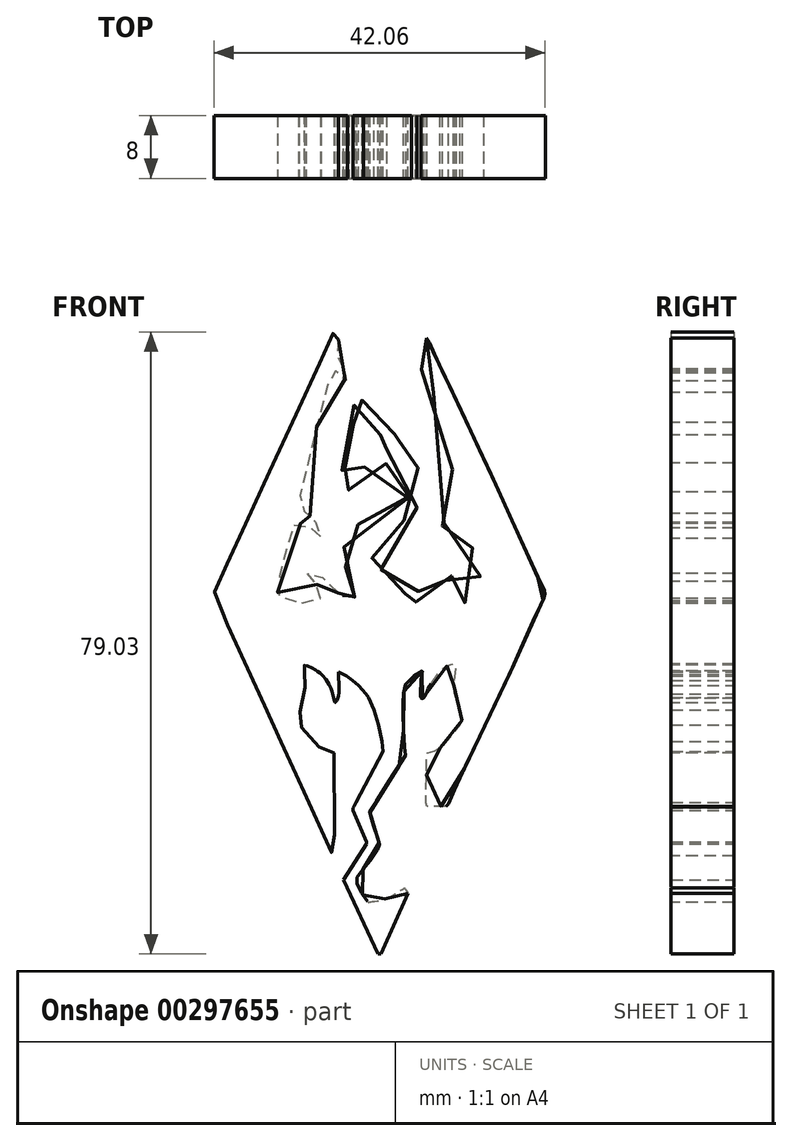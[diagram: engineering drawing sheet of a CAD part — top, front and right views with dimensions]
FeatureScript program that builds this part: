
annotation { "Feature Type Name" : "Feature", "Feature Type Description" : "" }
export const myFeature = defineFeature(function(context is Context, id is Id, definition is map)
    precondition{}
    {
        {
            var Q0;
            Q0=qCreatedBy(makeId("Front.planeOp"),FACE);
            var sketch = newSketch(context, id + "F0", { "sketchPlane" : qUnion([Q0])});
            skLineSegment(sketch, "E0", {"start": v(-80, 80.48) * mm, "end": v(-80, 0) * mm});
            skLineSegment(sketch, "E1", {"start": v(-80, 0) * mm, "end": v(0, 0) * mm});
            skLineSegment(sketch, "E2", {"start": v(0, 0) * mm, "end": v(0, 82.9) * mm});
            skLineSegment(sketch, "E3", {"start": v(0, 82.9) * mm, "end": v(-80, 80.48) * mm});
            skLineSegment(sketch, "E4", {"start": v(-24.18, 7.7) * mm, "end": v(-27.61, 0) * mm});
            skLineSegment(sketch, "E5", {"start": v(-27.61, 0) * mm, "end": v(-27.98, 0) * mm});
            skLineSegment(sketch, "E6", {"start": v(-27.98, 0) * mm, "end": v(-32.38, 9.42) * mm});
            skLineSegment(sketch, "E7", {"start": v(-32.38, 9.42) * mm, "end": v(-31.33, 11.07) * mm});
            skLineSegment(sketch, "E8", {"start": v(-31.33, 11.07) * mm, "end": v(-29.48, 13.96) * mm});
            skLineSegment(sketch, "E9", {"start": v(-29.48, 14.25) * mm, "end": v(-29.48, 13.96) * mm});
            skLineSegment(sketch, "E10", {"start": v(-29.48, 14.25) * mm, "end": v(-31.07, 18.02) * mm});
            skLineSegment(sketch, "E11", {"start": v(-31.07, 18.02) * mm, "end": v(-31.16, 18.24) * mm});
            skLineSegment(sketch, "E12", {"start": v(-31.16, 18.24) * mm, "end": v(-31.16, 18.45) * mm});
            skLineSegment(sketch, "E13", {"start": v(-31.16, 18.45) * mm, "end": v(-31.16, 18.6) * mm});
            skLineSegment(sketch, "E14", {"start": v(-31.16, 18.6) * mm, "end": v(-31.07, 18.79) * mm});
            skLineSegment(sketch, "E15", {"start": v(-31.07, 18.79) * mm, "end": v(-30.8, 19.3) * mm});
            skLineSegment(sketch, "E16", {"start": v(-30.8, 19.3) * mm, "end": v(-28.86, 22.93) * mm});
            skLineSegment(sketch, "E17", {"start": v(-28.86, 22.93) * mm, "end": v(-27.47, 25.54) * mm});
            skLineSegment(sketch, "E18", {"start": v(-27.47, 25.54) * mm, "end": v(-27.38, 25.7) * mm});
            skLineSegment(sketch, "E19", {"start": v(-27.38, 25.7) * mm, "end": v(-27.52, 27) * mm});
            skLineSegment(sketch, "E20", {"start": v(-27.52, 27) * mm, "end": v(-27.94, 29.12) * mm});
            skLineSegment(sketch, "E21", {"start": v(-27.94, 29.12) * mm, "end": v(-28.54, 31.02) * mm});
            skLineSegment(sketch, "E22", {"start": v(-28.54, 31.02) * mm, "end": v(-29.21, 32.62) * mm});
            skLineSegment(sketch, "E23", {"start": v(-29.21, 32.62) * mm, "end": v(-29.54, 33.06) * mm});
            skLineSegment(sketch, "E24", {"start": v(-29.54, 33.06) * mm, "end": v(-30.51, 34.14) * mm});
            skLineSegment(sketch, "E25", {"start": v(-30.51, 34.14) * mm, "end": v(-31.27, 34.78) * mm});
            skLineSegment(sketch, "E26", {"start": v(-31.27, 34.78) * mm, "end": v(-32.03, 35.3) * mm});
            skLineSegment(sketch, "E27", {"start": v(-32.03, 35.3) * mm, "end": v(-32.37, 35.52) * mm});
            skLineSegment(sketch, "E28", {"start": v(-32.37, 35.52) * mm, "end": v(-33.04, 35.8) * mm});
            skLineSegment(sketch, "E29", {"start": v(-33.04, 35.8) * mm, "end": v(-33.04, 35.52) * mm});
            skFitSpline(sketch, "E30", {"points": [v(-33.04, 35.52) * mm, v(-32.98, 34.7) * mm, v(-32.96, 34.28) * mm, v(-32.95, 33.57) * mm, v(-32.99, 33.2) * mm, v(-33.1, 32.52) * mm, v(-33.44, 31.92) * mm, v(-33.55, 32.17) * mm, v(-33.77, 33.03) * mm, v(-33.95, 33.58) * mm, v(-34.23, 34.24) * mm, v(-35.06, 35.42) * mm, v(-35.42, 35.72) * mm, v(-35.72, 35.94) * mm, v(-36.01, 36.14) * mm, v(-36.88, 36.6) * mm, v(-37.35, 36.68) * mm, v(-37.34, 36.34) * mm, v(-37.33, 35.98) * mm], "startDerivative": vector(1.1, -13.67) * mm, "endDerivative": vector(-0.4, -7.76) * mm});
            skFitSpline(sketch, "E31", {"points": [v(-37.33, 35.98) * mm, v(-37.29, 35.2) * mm, v(-37.3, 34.9) * mm, v(-37.3, 33.86) * mm, v(-37.55, 32.48) * mm, v(-37.95, 30.55) * mm, v(-38.08, 30.04) * mm, v(-38.02, 29.4) * mm, v(-37.45, 28.4) * mm, v(-35.92, 26.66) * mm, v(-35, 26.05) * mm, v(-33.88, 25.65) * mm, v(-33.68, 25.62) * mm, v(-33.6, 25.5) * mm, v(-33.56, 24.38) * mm, v(-33.57, 22.1) * mm, v(-33.56, 19.26) * mm, v(-33.56, 16.86) * mm, v(-33.57, 15.3) * mm, v(-33.59, 12.55) * mm, v(-33.7, 12.5) * mm, v(-34.23, 13.62) * mm, v(-34.61, 14.45) * mm, v(-36.12, 17.77) * mm, v(-37.28, 20.27) * mm, v(-37.7, 21.24) * mm, v(-39.07, 24.23) * mm, v(-40.42, 27.19) * mm, v(-41.69, 30) * mm, v(-48.6, 45) * mm, v(-48.82, 45.7) * mm, v(-48.48, 46.87) * mm, v(-47.1, 49.7) * mm, v(-44.84, 54.6) * mm, v(-40.78, 63.44) * mm, v(-36.52, 72.67) * mm, v(-34.17, 77.84) * mm, v(-33.71, 78.9) * mm, v(-33.66, 78.99) * mm, v(-33.6, 79.03) * mm, v(-33.46, 78.93) * mm, v(-33.04, 78.2) * mm, v(-33.03, 78.07) * mm, v(-33.19, 77.47) * mm, v(-33.22, 77.05) * mm, v(-33.2, 76.03) * mm, v(-32.87, 75.2) * mm, v(-32.62, 74.78) * mm, v(-32.14, 74) * mm, v(-31.95, 73.61) * mm, v(-31.9, 73.24) * mm, v(-32, 72.82) * mm, v(-32.05, 72.81) * mm, v(-32.36, 73.33) * mm, v(-32.86, 73.85) * mm, v(-33.24, 74.06) * mm, v(-34.01, 73.82) * mm, v(-34.36, 72.94) * mm, v(-34.5, 71.9) * mm, v(-35.29, 68.9) * mm, v(-36.16, 65.5) * mm, v(-37.52, 59.86) * mm, v(-38, 57.65) * mm, v(-37.95, 57.04) * mm, v(-37.54, 56.43) * mm, v(-36.92, 55.87) * mm, v(-36.46, 55.5) * mm, v(-36.02, 55) * mm, v(-35.6, 54.43) * mm, v(-35.32, 53.67) * mm, v(-35.29, 53.11) * mm, v(-35.36, 52.79) * mm, v(-36.14, 53.74) * mm, v(-36.55, 54.12) * mm, v(-37.4, 54.59) * mm, v(-38.14, 54.7) * mm, v(-38.8, 54.36) * mm, v(-39.09, 53.57) * mm, v(-39.5, 51.83) * mm, v(-40.14, 49.41) * mm, v(-40.77, 46.9) * mm, v(-40.76, 45.95) * mm, v(-40.58, 45.52) * mm, v(-39.53, 44.85) * mm, v(-37.8, 44.57) * mm, v(-36.5, 44.7) * mm, v(-35.43, 45.14) * mm, v(-35.23, 45.3) * mm, v(-35.34, 46.05) * mm, v(-35.8, 47) * mm, v(-36.94, 48.09) * mm, v(-37.15, 48.2) * mm, v(-37.17, 48.26) * mm, v(-37.11, 48.3) * mm, v(-36.92, 48.32) * mm, v(-36.63, 48.3) * mm, v(-36.24, 48.24) * mm, v(-35.15, 47.85) * mm, v(-34.71, 47.6) * mm, v(-33.55, 46.55) * mm, v(-32.76, 45.3) * mm, v(-32.52, 44.85) * mm, v(-32.5, 45.08) * mm, v(-32.6, 45.86) * mm, v(-33.03, 47.07) * mm, v(-33.18, 47.3) * mm, v(-33.14, 47.33) * mm, v(-32.96, 47.32) * mm, v(-31.78, 46.5) * mm, v(-31.39, 46.03) * mm, v(-30.87, 45.18) * mm, v(-30.84, 45.16) * mm, v(-30.8, 45.2) * mm, v(-30.85, 45.47) * mm, v(-30.94, 45.92) * mm, v(-31.37, 47.14) * mm, v(-31.6, 47.7) * mm, v(-32.1, 49.03) * mm, v(-32.27, 49.77) * mm, v(-32.4, 50.67) * mm, v(-32.14, 52.44) * mm, v(-31.11, 54.04) * mm, v(-30.16, 54.76) * mm, v(-27.34, 55.99) * mm, v(-27.32, 55.97) * mm, v(-25.95, 56.54) * mm, v(-24.17, 57.9) * mm, v(-23.9, 58.63) * mm, v(-23.8, 59.6) * mm, v(-24.2, 60.66) * mm, v(-25.45, 61.8) * mm, v(-27.07, 62.3) * mm, v(-28.93, 62.28) * mm, v(-30.29, 61.35) * mm, v(-31.73, 59.56) * mm, v(-31.71, 59.16) * mm, v(-31.82, 58.83) * mm, v(-32.07, 58.72) * mm, v(-32.42, 58.98) * mm, v(-32.82, 59.56) * mm, v(-32.94, 60.42) * mm, v(-32.93, 61.08) * mm, v(-32.43, 61.6) * mm, v(-32.07, 62.1) * mm, v(-32.2, 63.44) * mm, v(-32.06, 63.88) * mm, v(-30.81, 66.02) * mm, v(-30.83, 66.11) * mm, v(-31.14, 67.52) * mm, v(-31.08, 69.33) * mm, v(-30.77, 70.55) * mm, v(-30.18, 71.15) * mm, v(-29.87, 71.31) * mm, v(-29.96, 70.95) * mm, v(-30, 68.91) * mm, v(-29.33, 67.01) * mm, v(-28.97, 66.13) * mm, v(-26.27, 66.02) * mm, v(-24.74, 66.37) * mm, v(-24.14, 67) * mm, v(-23.89, 67.52) * mm, v(-23.84, 66.58) * mm, v(-25.13, 65.44) * mm, v(-26.81, 64.31) * mm, v(-26.93, 63.97) * mm, v(-26.38, 63.74) * mm, v(-24.05, 62.75) * mm, v(-22.63, 61.29) * mm, v(-22.24, 59.6) * mm, v(-22.4, 58.14) * mm, v(-23.9, 55.67) * mm, v(-26.38, 54.44) * mm, v(-28.06, 53.6) * mm, v(-29.13, 52.16) * mm, v(-28.84, 50.4) * mm, v(-26.98, 48.2) * mm, v(-25.69, 46.75) * mm, v(-24.9, 45.15) * mm, v(-24.49, 45.8) * mm, v(-23.23, 47.06) * mm, v(-22.49, 47.3) * mm, v(-22.56, 46.86) * mm, v(-23.27, 44.97) * mm, v(-23.29, 44.63) * mm, v(-22.9, 45.27) * mm, v(-21.8, 46.93) * mm, v(-19.72, 48.18) * mm, v(-18.48, 48.26) * mm, v(-18.7, 48.03) * mm, v(-20.08, 46.63) * mm, v(-20.22, 45.45) * mm, v(-20.19, 45.32) * mm, v(-18.46, 44.66) * mm, v(-16.2, 44.83) * mm, v(-14.7, 46) * mm, v(-15.32, 48.8) * mm, v(-16.09, 51.97) * mm, v(-16.73, 54.24) * mm, v(-17.16, 54.64) * mm, v(-18.1, 54.77) * mm, v(-19.81, 54.13) * mm, v(-19.31, 55.22) * mm, v(-17.91, 56.7) * mm, v(-17.77, 58.71) * mm, v(-18.74, 62.38) * mm, v(-21.58, 73.61) * mm, v(-22.03, 74.25) * mm, v(-22.62, 74.18) * mm, v(-22.98, 73.8) * mm, v(-23, 74.42) * mm, v(-22.45, 75.67) * mm, v(-22.56, 77.26) * mm, v(-21.88, 78.27) * mm, v(-21.35, 77.4) * mm, v(-15.69, 65.35) * mm, v(-6.79, 45.97) * mm, v(-6.77, 45.93) * mm, v(-6.85, 45.4) * mm, v(-6.97, 45.17) * mm, v(-11.44, 35.34) * mm, v(-19.12, 18.83) * mm, v(-19.15, 18.76) * mm, v(-21.8, 18.74) * mm, v(-21.88, 18.74) * mm, v(-21.84, 25.54) * mm, v(-21.84, 25.56) * mm, v(-20.46, 25.94) * mm, v(-17.97, 28.65) * mm, v(-17.37, 29.66) * mm, v(-18.16, 32.55) * mm, v(-18.31, 34.82) * mm, v(-18.24, 36.8) * mm, v(-20.56, 35.45) * mm, v(-22.31, 32.47) * mm, v(-22.52, 32.5) * mm, v(-22.62, 33.2) * mm, v(-22.36, 35.98) * mm, v(-22.35, 35.98) * mm, v(-24.15, 34.76) * mm, v(-24.77, 32.77) * mm, v(-24.84, 30.33) * mm, v(-24.54, 25.36) * mm, v(-24.66, 24.97) * mm, v(-29.03, 18.2) * mm, v(-29.06, 18.04) * mm, v(-28.65, 16.6) * mm, v(-27.85, 14.08) * mm, v(-27.85, 13.69) * mm, v(-29.4, 11.35) * mm, v(-30.7, 9.62) * mm, v(-30.5, 8.59) * mm, v(-29.26, 6.58) * mm, v(-29.03, 6.61) * mm, v(-27.05, 7) * mm, v(-24.62, 8.38) * mm, v(-24.6, 8.36) * mm, v(-24.18, 7.7) * mm], "startDerivative": vector(20.38, -301.3) * mm, "endDerivative": vector(195.78, -290.3) * mm});
            skLineSegment(sketch, "E32", {"start": v(-33.03, 78.07) * mm, "end": v(-21.88, 78.27) * mm});
            skSolve(sketch);
        }
        {
            var Q0;
            Q0=makeQuery(id+"F0.imprint","IMPRINT",FACE,{"disambiguationData":[TD([[makeQuery(id+"F0.imprint","IMPRINT",EDGE,{"derivedFrom":sQuery(id+"F0.wireOp",EDGE,"E4")}),-1.0]])]});
            extrude(context, id + "F1", {"entities" : qUnion([Q0]), "depth" : 8 * mm});
        }
    });
